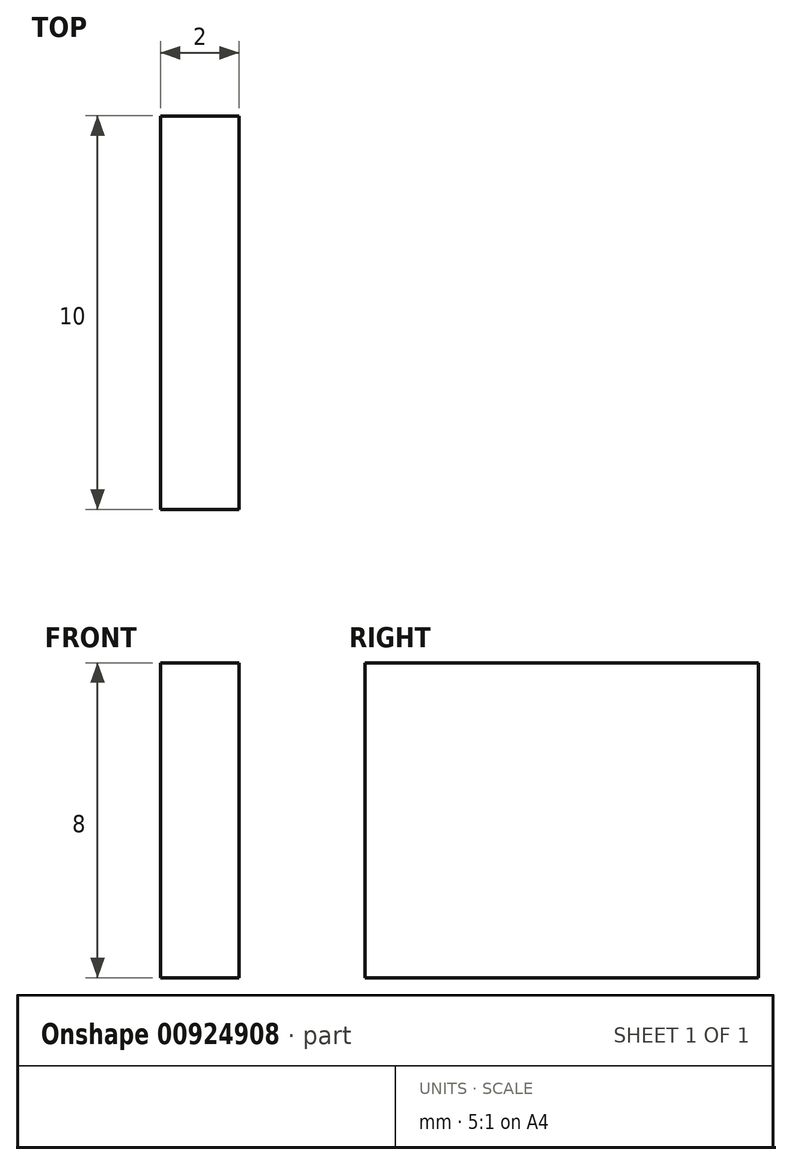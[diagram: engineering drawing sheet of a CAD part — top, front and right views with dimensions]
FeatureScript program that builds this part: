
annotation { "Feature Type Name" : "Feature", "Feature Type Description" : "" }
export const myFeature = defineFeature(function(context is Context, id is Id, definition is map)
    precondition{}
    {
        {
            var Q0;
            Q0=qCreatedBy(makeId("Right.planeOp"),FACE);
            var sketch = newSketch(context, id + "F0", { "sketchPlane" : qUnion([Q0])});
            skLineSegment(sketch, "E0.bottom", {"start": v(-6.74, 21.14) * mm, "end": v(-16.74, 21.14) * mm});
            skLineSegment(sketch, "E0.top", {"start": v(-6.74, 13.14) * mm, "end": v(-16.74, 13.14) * mm});
            skLineSegment(sketch, "E0.left", {"start": v(-6.74, 21.14) * mm, "end": v(-6.74, 13.14) * mm});
            skLineSegment(sketch, "E0.right", {"start": v(-16.74, 21.14) * mm, "end": v(-16.74, 13.14) * mm});
            skSolve(sketch);
        }
        {
            var Q0;
            Q0=makeQuery(id+"F0.imprint","IMPRINT",FACE,{"disambiguationData":[TD([[makeQuery(id+"F0.imprint","IMPRINT",EDGE,{"derivedFrom":sQuery(id+"F0.wireOp",EDGE,"E0.bottom")}),1.0]])]});
            extrude(context, id + "F1", {"entities" : qUnion([Q0]), "depth" : 2 * mm, "offsetDistance" : 25 * mm});
        }
    });
